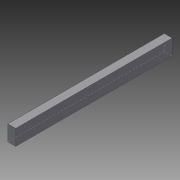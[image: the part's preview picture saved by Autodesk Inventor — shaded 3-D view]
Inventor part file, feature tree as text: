
AUTODESK INVENTOR PART (.ipt)
format: ipt  version: 2016 (Build 200138000, 138)  size: 70,144 bytes
history: native  units: mm
features: extrude x1, sketch x1
ambient origin geometry x8: Origin, YZ Plane, XZ Plane, XY Plane, X Axis, Y Axis, Z Axis, Center Point
bodies: 实体1 (feature_tree)
feature tree (2):
  extrude  "拉伸1"  Depth=40.0mm
  sketch  "草图1"  dims[d0=20.0mm d1=40.0mm d2=400.0mm d3=0.0mm]
